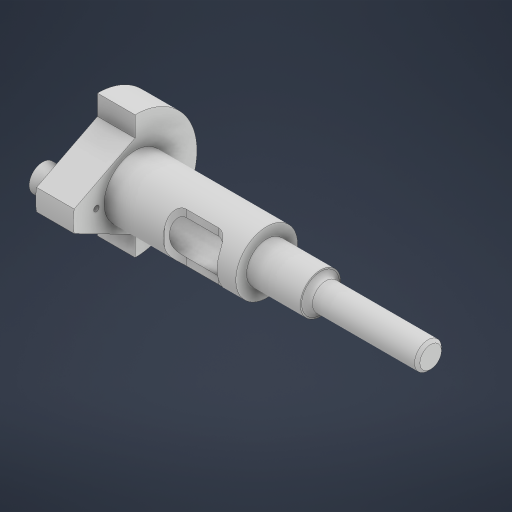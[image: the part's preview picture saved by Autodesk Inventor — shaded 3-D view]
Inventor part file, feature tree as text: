
AUTODESK INVENTOR PART (.ipt)
format: ipt  version: 2023 (Build 270158000, 158)  size: 286,720 bytes
history: native  units: mm
features: sketch x6, extrude x3, other x2, hole x2, revolve x1, chamfer x1
ambient origin geometry x8: Origin, YZ Plane, XZ Plane, XY Plane, X Axis, Y Axis, Z Axis, Center Point
bodies: Body1 (feature_tree)
feature tree (15):
  other  "Bryła1"
  revolve  "Obrót1"
  hole  "Otwór1"  [1 undecoded]
  chamfer  "Faza1"  Distance=23.0mm
  other  "Zaokrąglenie powierzchni1"
  extrude  "Wyciągnięcie proste1"  Depth=49.0mm
  extrude  "Wyciągnięcie proste2"  Depth=11.5mm
  hole  "Otwór2"  [1 undecoded]
  extrude  "Wyciągnięcie proste3"  Depth=7.5mm
  sketch  "Szkic1"
  sketch  "Szkic2"
  sketch  "Szkic3"
  sketch  "Szkic4"
  sketch  "Szkic5"
  sketch  "Szkic6"
note: 2 required parameter values undecoded (feature->parameter linkage not recoverable at this tier; creation-order binding heuristic only, values carry confidence <= 0.55)
